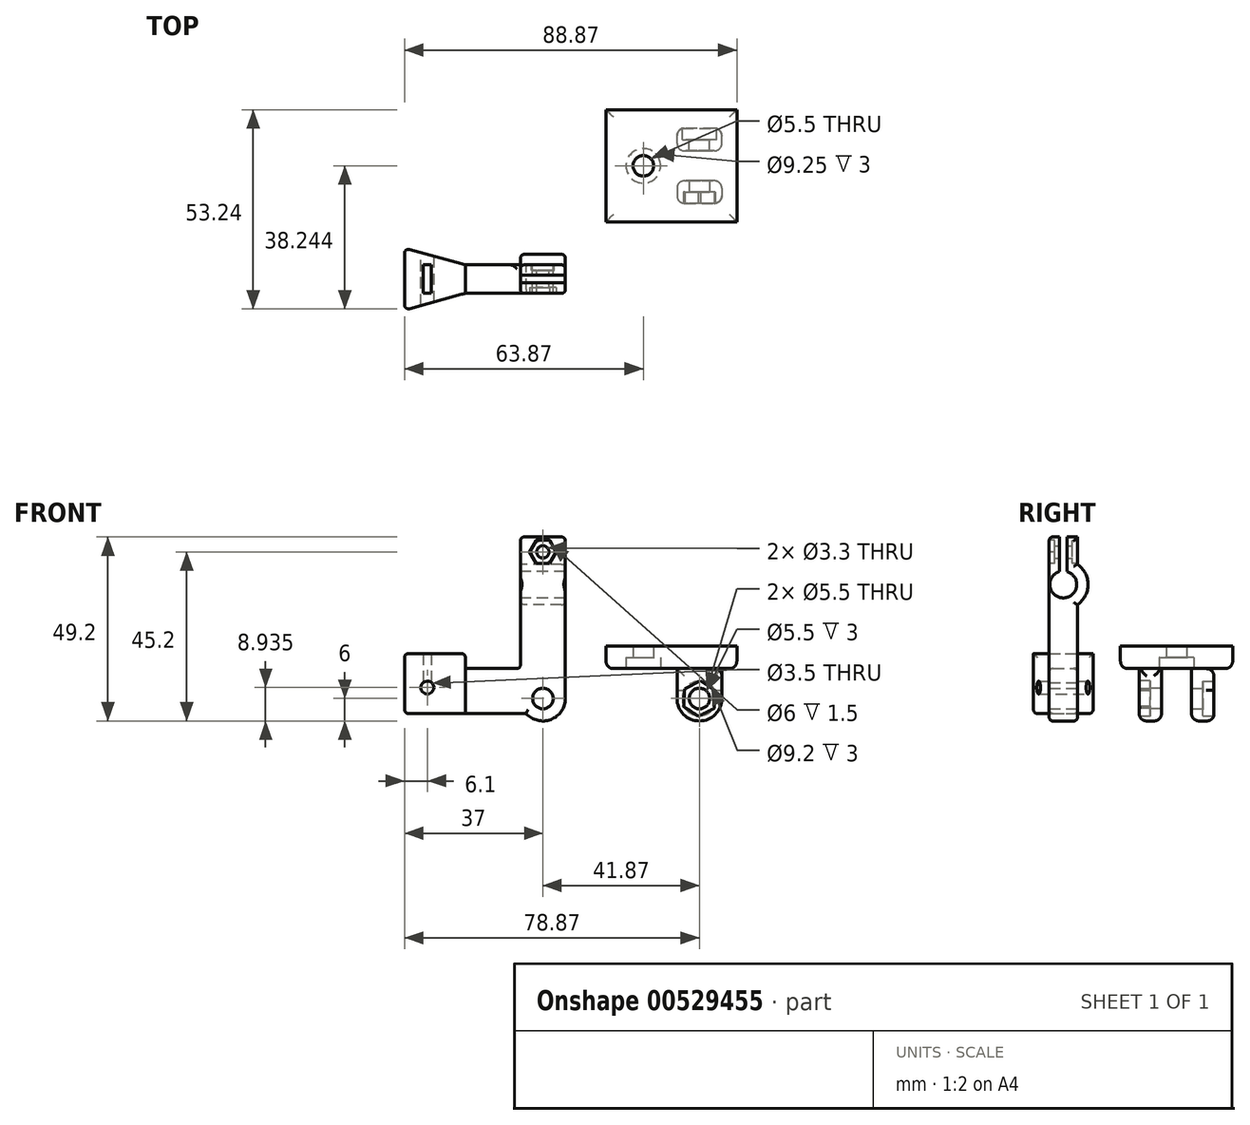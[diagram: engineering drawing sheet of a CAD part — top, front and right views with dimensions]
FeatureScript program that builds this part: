
annotation { "Feature Type Name" : "Feature", "Feature Type Description" : "" }
export const myFeature = defineFeature(function(context is Context, id is Id, definition is map)
    precondition{}
    {
        {
            assignVariable(context, id + "F0", {"name" : "pivot_w", "anyValue" : 8});
        }
        {
            assignVariable(context, id + "F1", {"name" : "hole_d", "anyValue" : 7.2});
        }
        {
            var Q0;
            Q0=qCreatedBy(makeId("Top.planeOp"),FACE);
            var sketch = newSketch(context, id + "F2", { "sketchPlane" : qUnion([Q0])});
            skLineSegment(sketch, "E0.bottom", {"start": v(-46.75, 41.48) * mm, "end": v(-11.75, 41.48) * mm});
            skLineSegment(sketch, "E0.top", {"start": v(-46.75, 11.48) * mm, "end": v(-11.75, 11.48) * mm});
            skLineSegment(sketch, "E0.left", {"start": v(-46.75, 41.48) * mm, "end": v(-46.75, 11.48) * mm});
            skLineSegment(sketch, "E0.right", {"start": v(-11.75, 41.48) * mm, "end": v(-11.75, 11.48) * mm});
            skPoint(sketch, "E1", {"position": v(-36.75, 26.48) * mm});
            skPoint(sketch, "E2", {"position": v(-46.75, 26.48) * mm});
            skLineSegment(sketch, "E3", {"start": v(-46.75, 26.48) * mm, "end": v(-36.75, 26.48) * mm, "construction": true});
            skPoint(sketch, "E4", {"position": v(-21.75, 30.48) * mm});
            skPoint(sketch, "E5", {"position": v(-21.75, 22.48) * mm});
            skLineSegment(sketch, "E6", {"start": v(-21.75, 30.48) * mm, "end": v(-21.75, 41.48) * mm, "construction": true});
            skLineSegment(sketch, "E7", {"start": v(-21.75, 22.48) * mm, "end": v(-21.75, 11.48) * mm, "construction": true});
            skLineSegment(sketch, "E8", {"start": v(-21.75, 30.48) * mm, "end": v(-11.75, 30.48) * mm, "construction": true});
            skSolve(sketch);
        }
        {
            var Q0;
            Q0=makeQuery(id+"F2.imprint","IMPRINT",FACE,{"disambiguationData":[TD([[makeQuery(id+"F2.imprint","IMPRINT",EDGE,{"derivedFrom":sQuery(id+"F2.wireOp",EDGE,"E0.bottom")}),-1.0]])]});
            extrude(context, id + "F3", {"entities" : qUnion([Q0]), "depth" : 6 * mm, "offsetDistance" : 25 * mm});
        }
        {
            var Q0;
            Q0=sQuery(id+"F2.wireOp",VERTEX,"E1");
            var Q1;
            Q1=makeQuery(id+"F3.opExtrude","SWEPT_BODY",BODY,{"disambiguationData":[OSD([sQuery(id+"F2.wireOp",EDGE,"E0.bottom"),sQuery(id+"F2.wireOp",EDGE,"E0.top"),sQuery(id+"F2.wireOp",EDGE,"E0.left"),sQuery(id+"F2.wireOp",EDGE,"E0.right")])]});
            hole(context, id + "F4", {"style" : HoleStyle.C_BORE, "endStyle" : HoleEndStyle.BLIND, "oppositeDirection" : true, "holeDiameter" : 5.5 * mm, "cBoreDiameter" : 9.25 * mm, "cBoreDepth" : 3 * mm, "holeDepth" : 12.9 * mm, "isTappedThrough" : true, "tappedDepth" : 10.5 * mm, "tapClearance" : 3, "locations" : qUnion([Q0]), "scope" : qUnion([Q1])});
        }
        {
            var Q0;
            Q0=qCreatedBy(makeId("Front.planeOp"),FACE);
            var sketch = newSketch(context, id + "F5", { "sketchPlane" : qUnion([Q0])});
            skCircle(sketch, "E9", {"center": v(-35.54, -8) * mm, "radius": 6 * mm});
            skLineSegment(sketch, "E10.bottom", {"start": v(-29.54, 0) * mm, "end": v(-41.54, 0) * mm});
            skLineSegment(sketch, "E10.top", {"start": v(-29.54, -8) * mm, "end": v(-41.54, -8) * mm});
            skLineSegment(sketch, "E10.left", {"start": v(-29.54, 0) * mm, "end": v(-29.54, -8) * mm});
            skLineSegment(sketch, "E10.right", {"start": v(-41.54, 0) * mm, "end": v(-41.54, -8) * mm});
            skCircle(sketch, "E11", {"center": v(-17.83, -8.12) * mm, "radius": 6 * mm});
            skLineSegment(sketch, "E12.bottom", {"start": v(-11.83, -0.12) * mm, "end": v(-23.83, -0.12) * mm});
            skLineSegment(sketch, "E12.top", {"start": v(-11.83, -8.12) * mm, "end": v(-23.83, -8.12) * mm});
            skLineSegment(sketch, "E12.left", {"start": v(-11.83, -0.12) * mm, "end": v(-11.83, -8.12) * mm});
            skLineSegment(sketch, "E12.right", {"start": v(-23.83, -0.12) * mm, "end": v(-23.83, -8.12) * mm});
            skCircle(sketch, "E13", {"center": v(-35.54, -8) * mm, "radius": 2.75 * mm});
            skCircle(sketch, "E14", {"center": v(-35.54, -8) * mm, "radius": 4.6 * mm});
            skCircle(sketch, "E15", {"center": v(-17.83, -8.12) * mm, "radius": 2.75 * mm});
            skCircle(sketch, "E16.cCircle", {"center": v(-17.83, -8.12) * mm, "radius": 4.1 * mm, "construction": true});
            skLineSegment(sketch, "E16.0", {"start": v(-17.54, -12.85) * mm, "end": v(-21.78, -10.74) * mm});
            skLineSegment(sketch, "E16.1", {"start": v(-21.78, -10.74) * mm, "end": v(-22.07, -6.01) * mm});
            skLineSegment(sketch, "E16.2", {"start": v(-22.07, -6.01) * mm, "end": v(-18.12, -3.4) * mm});
            skLineSegment(sketch, "E16.3", {"start": v(-18.12, -3.4) * mm, "end": v(-13.89, -5.5) * mm});
            skLineSegment(sketch, "E16.4", {"start": v(-13.89, -5.5) * mm, "end": v(-13.6, -10.23) * mm});
            skLineSegment(sketch, "E16.5", {"start": v(-13.6, -10.23) * mm, "end": v(-17.54, -12.85) * mm});
            skPoint(sketch, "E16.0.midPoint", {"position": v(-19.66, -11.8) * mm});
            skCircle(sketch, "E17", {"center": v(-63.62, -8) * mm, "radius": 6 * mm});
            skLineSegment(sketch, "E18.bottom", {"start": v(-57.62, 35.2) * mm, "end": v(-69.62, 35.2) * mm});
            skLineSegment(sketch, "E18.top", {"start": v(-57.62, -8) * mm, "end": v(-69.62, -8) * mm});
            skLineSegment(sketch, "E18.left", {"start": v(-57.62, 35.2) * mm, "end": v(-57.62, -8) * mm});
            skLineSegment(sketch, "E18.right", {"start": v(-69.62, 35.2) * mm, "end": v(-69.62, -8) * mm});
            skCircle(sketch, "E19", {"center": v(-63.62, -8) * mm, "radius": 2.75 * mm});
            skLineSegment(sketch, "E20.bottom", {"start": v(-69.62, -8) * mm, "end": v(-100.62, -8) * mm});
            skLineSegment(sketch, "E20.right", {"start": v(-100.62, -8) * mm, "end": v(-100.62, 0) * mm});
            skLineSegment(sketch, "E21.top", {"start": v(-100.62, 4) * mm, "end": v(-84.62, 4) * mm});
            skLineSegment(sketch, "E21.left", {"start": v(-100.62, 0) * mm, "end": v(-100.62, 4) * mm});
            skLineSegment(sketch, "E21.right", {"start": v(-84.62, 0) * mm, "end": v(-84.62, 4) * mm});
            skLineSegment(sketch, "E22", {"start": v(-84.62, 0) * mm, "end": v(-69.62, 0) * mm});
            skLineSegment(sketch, "E23.bottom", {"start": v(-95.62, 4) * mm, "end": v(-93.42, 4) * mm});
            skLineSegment(sketch, "E23.top", {"start": v(-95.62, -3.7) * mm, "end": v(-93.42, -3.7) * mm});
            skLineSegment(sketch, "E23.left", {"start": v(-95.62, 4) * mm, "end": v(-95.62, -3.7) * mm});
            skLineSegment(sketch, "E23.right", {"start": v(-93.42, 4) * mm, "end": v(-93.42, -3.7) * mm});
            skPoint(sketch, "E24", {"position": v(-63.62, 31.2) * mm});
            skPoint(sketch, "E24.positionSnap0", {"position": v(-63.62, 35.2) * mm});
            skLineSegment(sketch, "E25.bottom", {"start": v(-67.67, 25) * mm, "end": v(-66.17, 25) * mm});
            skLineSegment(sketch, "E25.top", {"start": v(-67.67, 20) * mm, "end": v(-66.17, 20) * mm});
            skLineSegment(sketch, "E25.left", {"start": v(-67.67, 25) * mm, "end": v(-67.67, 20) * mm});
            skLineSegment(sketch, "E25.right", {"start": v(-66.17, 25) * mm, "end": v(-66.17, 20) * mm});
            skLineSegment(sketch, "E26.1.0.0", {"start": v(-64.37, 20) * mm, "end": v(-62.87, 20) * mm});
            skLineSegment(sketch, "E26.1.0.1", {"start": v(-62.87, 25) * mm, "end": v(-62.87, 20) * mm});
            skLineSegment(sketch, "E26.1.0.2", {"start": v(-64.37, 25) * mm, "end": v(-64.37, 20) * mm});
            skLineSegment(sketch, "E26.1.0.3", {"start": v(-64.37, 25) * mm, "end": v(-62.87, 25) * mm});
            skLineSegment(sketch, "E26.2.0.0", {"start": v(-61.07, 20) * mm, "end": v(-59.57, 20) * mm});
            skLineSegment(sketch, "E26.2.0.1", {"start": v(-59.57, 25) * mm, "end": v(-59.57, 20) * mm});
            skLineSegment(sketch, "E26.2.0.2", {"start": v(-61.07, 25) * mm, "end": v(-61.07, 20) * mm});
            skLineSegment(sketch, "E26.2.0.3", {"start": v(-61.07, 25) * mm, "end": v(-59.57, 25) * mm});
            skLineSegment(sketch, "E26.direction1", {"start": v(-67.67, 20) * mm, "end": v(-64.37, 20) * mm, "construction": true});
            skLineSegment(sketch, "E27", {"start": v(-64.94, 35.2) * mm, "end": v(-64.94, 25) * mm, "construction": true});
            skLineSegment(sketch, "E28", {"start": v(-67.67, 25) * mm, "end": v(-69.62, 25) * mm, "construction": true});
            skLineSegment(sketch, "E29", {"start": v(-59.57, 25) * mm, "end": v(-57.62, 25) * mm, "construction": true});
            skLineSegment(sketch, "E30", {"start": v(-67.67, 22.5) * mm, "end": v(-69.62, 22.5) * mm, "construction": true});
            skCircle(sketch, "E31", {"center": v(-94.52, -5.06) * mm, "radius": 1.75 * mm});
            skLineSegment(sketch, "E32", {"start": v(-68.1, -12) * mm, "end": v(-100.62, -12) * mm});
            skLineSegment(sketch, "E33", {"start": v(-100.62, -12) * mm, "end": v(-100.62, -8) * mm});
            skLineSegment(sketch, "E34", {"start": v(-100.62, -2) * mm, "end": v(-95.62, -2) * mm, "construction": true});
            skSolve(sketch);
        }
        {
            var Q0;
            Q0=makeQuery(id+"F5.imprint","IMPRINT",FACE,{"disambiguationData":[TD([[makeQuery(id+"F5.imprint","IMPRINT",EDGE,{"derivedFrom":sQuery(id+"F5.wireOp",EDGE,"E10.bottom")}),1.0]])]});
            var Q1;
            {var subQ0=sQuery(id+"F5.wireOp",EDGE,"E14");var subQ1=sQuery(id+"F5.wireOp",EDGE,"E10.top");var subQ2=makeQuery(id+"F5.imprint","INTERSECT",VERTEX,{"disambiguationData":[OD(0.0)],"derivedFrom":[subQ1,subQ0]});Q1=makeQuery(id+"F5.imprint","IMPRINT",FACE,{"disambiguationData":[TD([[makeQuery(id+"F5.imprint","IMPRINT",EDGE,{"disambiguationData":[TD([[subQ2,-1.0]])],"derivedFrom":subQ1}),-1.0]])]});}
            var Q2;
            {var subQ0=sQuery(id+"F5.wireOp",EDGE,"E10.top");var subQ4=sQuery(id+"F5.wireOp",EDGE,"E14");var subQ5=makeQuery(id+"F5.imprint","INTERSECT",VERTEX,{"disambiguationData":[OD(0.0)],"derivedFrom":[subQ0,subQ4]});Q2=makeQuery(id+"F5.imprint","IMPRINT",FACE,{"disambiguationData":[TD([[makeQuery(id+"F5.imprint","IMPRINT",EDGE,{"disambiguationData":[TD([[subQ5,1.0]])],"derivedFrom":subQ4}),-1.0]])]});}
            var Q3;
            {var subQ0=sQuery(id+"F5.wireOp",EDGE,"E14");var subQ1=sQuery(id+"F5.wireOp",EDGE,"E10.top");var subQ2=makeQuery(id+"F5.imprint","INTERSECT",VERTEX,{"disambiguationData":[OD(0.0)],"derivedFrom":[subQ1,subQ0]});Q3=makeQuery(id+"F5.imprint","IMPRINT",FACE,{"disambiguationData":[TD([[makeQuery(id+"F5.imprint","IMPRINT",EDGE,{"disambiguationData":[TD([[subQ2,-1.0]])],"derivedFrom":subQ1}),1.0]])]});}
            var Q4;
            {var subQ0=sQuery(id+"F5.wireOp",EDGE,"E10.top");var subQ4=sQuery(id+"F5.wireOp",EDGE,"E14");var subQ5=makeQuery(id+"F5.imprint","INTERSECT",VERTEX,{"disambiguationData":[OD(0.0)],"derivedFrom":[subQ0,subQ4]});Q4=makeQuery(id+"F5.imprint","IMPRINT",FACE,{"disambiguationData":[TD([[makeQuery(id+"F5.imprint","IMPRINT",EDGE,{"disambiguationData":[TD([[subQ5,-1.0]])],"derivedFrom":subQ4}),-1.0]])]});}
            var Q5;
            Q5=makeQuery(id+"F5.imprint","IMPRINT",FACE,{"disambiguationData":[TD([[makeQuery(id+"F5.imprint","IMPRINT",EDGE,{"derivedFrom":sQuery(id+"F5.wireOp",EDGE,"E12.bottom")}),1.0]])]});
            var Q6;
            {var subQ5=sQuery(id+"F5.wireOp",EDGE,"E16.2");Q6=makeQuery(id+"F5.imprint","IMPRINT",FACE,{"disambiguationData":[TD([[makeQuery(id+"F5.imprint","IMPRINT",EDGE,{"derivedFrom":subQ5}),1.0]])]});}
            var Q7;
            {var subQ0=sQuery(id+"F5.wireOp",EDGE,"E16.2");Q7=makeQuery(id+"F5.imprint","IMPRINT",FACE,{"disambiguationData":[TD([[makeQuery(id+"F5.imprint","IMPRINT",EDGE,{"derivedFrom":subQ0}),-1.0]])]});}
            var Q8;
            {var subQ8=sQuery(id+"F5.wireOp",EDGE,"E16.0");Q8=makeQuery(id+"F5.imprint","IMPRINT",FACE,{"disambiguationData":[TD([[makeQuery(id+"F5.imprint","IMPRINT",EDGE,{"derivedFrom":subQ8}),1.0]])]});}
            var Q9;
            {var subQ6=sQuery(id+"F5.wireOp",EDGE,"E16.0");Q9=makeQuery(id+"F5.imprint","IMPRINT",FACE,{"disambiguationData":[TD([[makeQuery(id+"F5.imprint","IMPRINT",EDGE,{"derivedFrom":subQ6}),-1.0]])]});}
            extrude(context, id + "F6", {"entities" : qUnion([Q0, Q1, Q2, Q3, Q4, Q5, Q6, Q7, Q8, Q9]), "depth" : 6 * mm, "offsetDistance" : 25 * mm});
        }
        {
            var Q0;
            {var subQ0=sQuery(id+"F5.wireOp",EDGE,"E16.2");Q0=makeQuery(id+"F5.imprint","IMPRINT",FACE,{"disambiguationData":[TD([[makeQuery(id+"F5.imprint","IMPRINT",EDGE,{"derivedFrom":subQ0}),-1.0]])]});}
            var Q1;
            {var subQ6=sQuery(id+"F5.wireOp",EDGE,"E16.0");Q1=makeQuery(id+"F5.imprint","IMPRINT",FACE,{"disambiguationData":[TD([[makeQuery(id+"F5.imprint","IMPRINT",EDGE,{"derivedFrom":subQ6}),-1.0]])]});}
            var Q2;
            {var subQ0=sQuery(id+"F5.wireOp",EDGE,"E14");var subQ1=sQuery(id+"F5.wireOp",EDGE,"E10.top");var subQ2=makeQuery(id+"F5.imprint","INTERSECT",VERTEX,{"disambiguationData":[OD(0.0)],"derivedFrom":[subQ1,subQ0]});Q2=makeQuery(id+"F5.imprint","IMPRINT",FACE,{"disambiguationData":[TD([[makeQuery(id+"F5.imprint","IMPRINT",EDGE,{"disambiguationData":[TD([[subQ2,-1.0]])],"derivedFrom":subQ1}),1.0]])]});}
            var Q3;
            {var subQ0=sQuery(id+"F5.wireOp",EDGE,"E14");var subQ1=sQuery(id+"F5.wireOp",EDGE,"E10.top");var subQ2=makeQuery(id+"F5.imprint","INTERSECT",VERTEX,{"disambiguationData":[OD(0.0)],"derivedFrom":[subQ1,subQ0]});Q3=makeQuery(id+"F5.imprint","IMPRINT",FACE,{"disambiguationData":[TD([[makeQuery(id+"F5.imprint","IMPRINT",EDGE,{"disambiguationData":[TD([[subQ2,-1.0]])],"derivedFrom":subQ1}),-1.0]])]});}
            extrude(context, id + "F7", {"entities" : qUnion([Q0, Q1, Q2, Q3]), "operationType" : NewBodyOperationType.REMOVE, "depth" : 3 * mm, "offsetDistance" : 25 * mm});
        }
        {
            var Q0;
            Q0=makeQuery(id+"F6.opExtrude","CAP_EDGE",EDGE,{"disambiguationData":[OSD([sQuery(id+"F5.wireOp",EDGE,"E10.bottom")])],"isStart":false});
            cPoint(context, id + "F8", {"entities" : qUnion([Q0]), "parameter" : 0.5});
        }
        {
            var Q0;
            Q0=makeQuery(id+"F6.opExtrude","SWEPT_BODY",BODY,{"disambiguationData":[OSD([sQuery(id+"F5.wireOp",EDGE,"E9"),sQuery(id+"F5.wireOp",EDGE,"E10.bottom"),sQuery(id+"F5.wireOp",EDGE,"E10.left"),sQuery(id+"F5.wireOp",EDGE,"E10.right"),sQuery(id+"F5.wireOp",EDGE,"E13")])]});
            var Q1;
            Q1=qCreatedBy(id+"F8",VERTEX);
            var Q2;
            Q2=sQuery(id+"F2.wireOp",VERTEX,"E6.start");
            transform(context, id + "F9", {"entities" : qUnion([Q0]), "transformType" : TransformType.TRANSLATION_ENTITY, "oppositeDirectionEntity" : false, "transformLine" : qUnion([Q1, Q2]), "makeCopy" : false});
        }
        {
            var Q0;
            Q0=makeQuery(id+"F6.opExtrude","SWEPT_BODY",BODY,{"disambiguationData":[OSD([sQuery(id+"F5.wireOp",EDGE,"E11"),sQuery(id+"F5.wireOp",EDGE,"E12.bottom"),sQuery(id+"F5.wireOp",EDGE,"E12.left"),sQuery(id+"F5.wireOp",EDGE,"E12.right"),sQuery(id+"F5.wireOp",EDGE,"E15")])]});
            var Q1;
            Q1=sQuery(id+"F5.wireOp",EDGE,"E12.left");
            transform(context, id + "F10", {"entities" : qUnion([Q0]), "transformType" : TransformType.ROTATION, "transformAxis" : qUnion([Q1]), "angle" : 180 * degree, "makeCopy" : false});
        }
        {
            var Q0;
            Q0=makeQuery(id+"F6.opExtrude","CAP_EDGE",EDGE,{"disambiguationData":[OSD([sQuery(id+"F5.wireOp",EDGE,"E12.bottom")])],"isStart":false});
            cPoint(context, id + "F11", {"entities" : qUnion([Q0]), "parameter" : 0.5});
        }
        {
            var Q0;
            Q0=makeQuery(id+"F6.opExtrude","SWEPT_BODY",BODY,{"disambiguationData":[OSD([sQuery(id+"F5.wireOp",EDGE,"E11"),sQuery(id+"F5.wireOp",EDGE,"E12.bottom"),sQuery(id+"F5.wireOp",EDGE,"E12.left"),sQuery(id+"F5.wireOp",EDGE,"E12.right"),sQuery(id+"F5.wireOp",EDGE,"E15")])]});
            var Q1;
            Q1=qCreatedBy(id+"F11",VERTEX);
            var Q2;
            Q2=sQuery(id+"F2.wireOp",VERTEX,"E7.start");
            transform(context, id + "F12", {"entities" : qUnion([Q0]), "transformType" : TransformType.TRANSLATION_ENTITY, "oppositeDirectionEntity" : false, "transformLine" : qUnion([Q1, Q2]), "makeCopy" : false});
        }
        {
            var Q0;
            {var subQ0=sQuery(id+"F5.wireOp",EDGE,"E18.top");var subQ4=sQuery(id+"F5.wireOp",EDGE,"E19");var subQ5=makeQuery(id+"F5.imprint","INTERSECT",VERTEX,{"disambiguationData":[OD(0.0)],"derivedFrom":[subQ0,subQ4]});Q0=makeQuery(id+"F5.imprint","IMPRINT",FACE,{"disambiguationData":[TD([[makeQuery(id+"F5.imprint","IMPRINT",EDGE,{"disambiguationData":[TD([[subQ5,1.0]])],"derivedFrom":subQ4}),-1.0]])]});}
            var Q1;
            {var subQ0=sQuery(id+"F5.wireOp",EDGE,"E18.top");var subQ4=sQuery(id+"F5.wireOp",EDGE,"E19");var subQ6=makeQuery(id+"F5.imprint","INTERSECT",VERTEX,{"disambiguationData":[OD(0.0)],"derivedFrom":[subQ0,subQ4]});Q1=makeQuery(id+"F5.imprint","IMPRINT",FACE,{"disambiguationData":[TD([[makeQuery(id+"F5.imprint","IMPRINT",EDGE,{"disambiguationData":[TD([[subQ6,-1.0]])],"derivedFrom":subQ4}),-1.0]])]});}
            var Q2;
            Q2=qSketchRegion(id+"F14",true);
            var Q3;
            {var subQ0=sQuery(id+"F5.wireOp",EDGE,"E18.bottom");Q3=makeQuery(id+"F5.imprint","IMPRINT",FACE,{"disambiguationData":[TD([[makeQuery(id+"F5.imprint","IMPRINT",EDGE,{"derivedFrom":subQ0}),1.0]])]});}
            var Q4;
            Q4=makeQuery(id+"F5.imprint","IMPRINT",FACE,{"disambiguationData":[TD([[makeQuery(id+"F5.imprint","IMPRINT",EDGE,{"derivedFrom":sQuery(id+"F5.wireOp",EDGE,"E26.2.0.0")}),1.0]])]});
            var Q5;
            Q5=makeQuery(id+"F5.imprint","IMPRINT",FACE,{"disambiguationData":[TD([[makeQuery(id+"F5.imprint","IMPRINT",EDGE,{"derivedFrom":sQuery(id+"F5.wireOp",EDGE,"E26.1.0.0")}),1.0]])]});
            var Q6;
            Q6=makeQuery(id+"F5.imprint","IMPRINT",FACE,{"disambiguationData":[TD([[makeQuery(id+"F5.imprint","IMPRINT",EDGE,{"derivedFrom":sQuery(id+"F5.wireOp",EDGE,"E25.bottom")}),-1.0]])]});
            var Q7;
            {var subQ0=sQuery(id+"F5.wireOp",EDGE,"E20.bottom");Q7=makeQuery(id+"F5.imprint","IMPRINT",FACE,{"disambiguationData":[TD([[makeQuery(id+"F5.imprint","IMPRINT",EDGE,{"derivedFrom":subQ0}),1.0]])]});}
            var Q8;
            {var subQ0=sQuery(id+"F5.wireOp",EDGE,"E21.right");Q8=makeQuery(id+"F5.imprint","IMPRINT",FACE,{"disambiguationData":[TD([[makeQuery(id+"F5.imprint","IMPRINT",EDGE,{"derivedFrom":subQ0}),1.0]])]});}
            var Q9;
            {var subQ6=sQuery(id+"F5.wireOp",EDGE,"E20.right");Q9=makeQuery(id+"F5.imprint","IMPRINT",FACE,{"disambiguationData":[TD([[makeQuery(id+"F5.imprint","IMPRINT",EDGE,{"derivedFrom":subQ6}),-1.0]])]});}
            extrude(context, id + "F13", {"entities" : qUnion([Q0, Q1, Q2, Q3, Q4, Q5, Q6, Q7, Q8, Q9]), "depth" : (getVariable(context, 'pivot_w') - 0.4) * mm, "offsetDistance" : 25 * mm});
        }
        {
            var Q0;
            Q0=makeQuery(id+"F13.opExtrude","SWEPT_FACE",FACE,{"disambiguationData":[OSD([sQuery(id+"F5.wireOp",EDGE,"E18.right")])]});
            var sketch = newSketch(context, id + "F14", { "sketchPlane" : qUnion([Q0])});
            skPoint(sketch, "E35", {"position": v(3.8, 22.5) * mm});
            skPoint(sketch, "E35.positionSnap0", {"position": v(3.8, 35.2) * mm});
            skPoint(sketch, "E36", {"position": v(0, 22.5) * mm});
            skLineSegment(sketch, "E37.bottom", {"start": v(2.8, 35.2) * mm, "end": v(4.8, 35.2) * mm});
            skLineSegment(sketch, "E37.top", {"start": v(2.8, 19.4) * mm, "end": v(4.8, 19.4) * mm});
            skLineSegment(sketch, "E37.left", {"start": v(2.8, 35.2) * mm, "end": v(2.8, 19.4) * mm});
            skLineSegment(sketch, "E37.right", {"start": v(4.8, 35.2) * mm, "end": v(4.8, 19.4) * mm});
            skLineSegment(sketch, "E38", {"start": v(2.8, 29.82) * mm, "end": v(0, 29.82) * mm});
            skLineSegment(sketch, "E39", {"start": v(4.8, 29.9) * mm, "end": v(7.6, 29.9) * mm});
            skLineSegment(sketch, "E40", {"start": v(3.8, 22.5) * mm, "end": v(0, 22.5) * mm, "construction": true});
            skCircle(sketch, "E41", {"center": v(3.8, 22.5) * mm, "radius": 6.6 * mm});
            skSolve(sketch);
        }
        {
            var Q0;
            {var subQ0=sQuery(id+"F14.wireOp",EDGE,"E41");var subQ1=makeQuery(id+"F13.opExtrude","CAP_EDGE",EDGE,{"disambiguationData":[OSD([sQuery(id+"F5.wireOp",EDGE,"E18.right")])],"isStart":true});var subQ2=makeQuery(id+"F14.imprint","INTERSECT",VERTEX,{"disambiguationData":[OD(0.0)],"derivedFrom":[subQ1,subQ0]});Q0=makeQuery(id+"F14.imprint","IMPRINT",FACE,{"disambiguationData":[TD([[makeQuery(id+"F14.imprint","IMPRINT",EDGE,{"disambiguationData":[TD([[subQ2,-1.0]])],"derivedFrom":subQ0}),1.0]])]});}
            var Q1;
            {var subQ0=sQuery(id+"F14.wireOp",EDGE,"E41");var subQ1=makeQuery(id+"F13.opExtrude","CAP_EDGE",EDGE,{"disambiguationData":[OSD([sQuery(id+"F5.wireOp",EDGE,"E18.right")])],"isStart":false});var subQ2=makeQuery(id+"F14.imprint","INTERSECT",VERTEX,{"disambiguationData":[OD(0.0)],"derivedFrom":[subQ1,subQ0]});Q1=makeQuery(id+"F14.imprint","IMPRINT",FACE,{"disambiguationData":[TD([[makeQuery(id+"F14.imprint","IMPRINT",EDGE,{"disambiguationData":[TD([[subQ2,1.0]])],"derivedFrom":subQ0}),1.0]])]});}
            extrude(context, id + "F15", {"entities" : qUnion([Q0, Q1]), "operationType" : NewBodyOperationType.ADD, "oppositeDirection" : true, "depth" : 12 * mm, "offsetDistance" : 25 * mm});
        }
        {
            var Q0;
            {var subQ4=sQuery(id+"F14.wireOp",EDGE,"E37.bottom");Q0=makeQuery(id+"F14.imprint","IMPRINT",FACE,{"disambiguationData":[TD([[makeQuery(id+"F14.imprint","IMPRINT",EDGE,{"derivedFrom":subQ4}),1.0]])]});}
            var Q1;
            {var subQ0=sQuery(id+"F14.wireOp",EDGE,"E37.top");Q1=makeQuery(id+"F14.imprint","IMPRINT",FACE,{"disambiguationData":[TD([[makeQuery(id+"F14.imprint","IMPRINT",EDGE,{"derivedFrom":subQ0}),1.0]])]});}
            extrude(context, id + "F16", {"entities" : qUnion([Q0, Q1]), "operationType" : NewBodyOperationType.REMOVE, "oppositeDirection" : true, "depth" : 12 * mm, "offsetDistance" : 25 * mm});
        }
        {
            var Q0;
            Q0=sQuery(id+"F14.wireOp",VERTEX,"E35");
            var Q1;
            Q1=makeQuery(id+"F13.opExtrude","SWEPT_BODY",BODY,{"disambiguationData":[OSD([sQuery(id+"F5.wireOp",EDGE,"E17"),sQuery(id+"F5.wireOp",EDGE,"E18.bottom"),sQuery(id+"F5.wireOp",EDGE,"E18.left"),sQuery(id+"F5.wireOp",EDGE,"E18.right"),sQuery(id+"F5.wireOp",EDGE,"E19"),sQuery(id+"F5.wireOp",EDGE,"E20.bottom"),sQuery(id+"F5.wireOp",EDGE,"E20.right"),sQuery(id+"F5.wireOp",EDGE,"E21.top"),sQuery(id+"F5.wireOp",EDGE,"E21.left"),sQuery(id+"F5.wireOp",EDGE,"E21.right"),sQuery(id+"F5.wireOp",EDGE,"E22"),sQuery(id+"F5.wireOp",EDGE,"E23.top"),sQuery(id+"F5.wireOp",EDGE,"E23.left"),sQuery(id+"F5.wireOp",EDGE,"E23.right"),sQuery(id+"F5.wireOp",EDGE,"E25.bottom"),sQuery(id+"F5.wireOp",EDGE,"E25.top"),sQuery(id+"F5.wireOp",EDGE,"E25.left"),sQuery(id+"F5.wireOp",EDGE,"E25.right"),sQuery(id+"F5.wireOp",EDGE,"E26.1.0.0"),sQuery(id+"F5.wireOp",EDGE,"E26.1.0.1"),sQuery(id+"F5.wireOp",EDGE,"E26.1.0.2"),sQuery(id+"F5.wireOp",EDGE,"E26.1.0.3"),sQuery(id+"F5.wireOp",EDGE,"E26.2.0.0"),sQuery(id+"F5.wireOp",EDGE,"E26.2.0.1"),sQuery(id+"F5.wireOp",EDGE,"E26.2.0.2"),sQuery(id+"F5.wireOp",EDGE,"E26.2.0.3")])]});
            hole(context, id + "F17", {"style" : HoleStyle.SIMPLE, "endStyle" : HoleEndStyle.BLIND, "holeDiameter" : (getVariable(context, 'hole_d')) * mm, "holeDepth" : 30 * mm, "isTappedThrough" : true, "tappedDepth" : 10.5 * mm, "tapClearance" : 3, "locations" : qUnion([Q0]), "scope" : qUnion([Q1])});
        }
        {
            var Q0;
            Q0=sQuery(id+"F5.wireOp",VERTEX,"E24");
            var Q1;
            Q1=makeQuery(id+"F13.opExtrude","SWEPT_BODY",BODY,{"disambiguationData":[OSD([sQuery(id+"F5.wireOp",EDGE,"E17"),sQuery(id+"F5.wireOp",EDGE,"E18.bottom"),sQuery(id+"F5.wireOp",EDGE,"E18.left"),sQuery(id+"F5.wireOp",EDGE,"E18.right"),sQuery(id+"F5.wireOp",EDGE,"E19"),sQuery(id+"F5.wireOp",EDGE,"E20.bottom"),sQuery(id+"F5.wireOp",EDGE,"E20.right"),sQuery(id+"F5.wireOp",EDGE,"E21.top"),sQuery(id+"F5.wireOp",EDGE,"E21.left"),sQuery(id+"F5.wireOp",EDGE,"E21.right"),sQuery(id+"F5.wireOp",EDGE,"E22"),sQuery(id+"F5.wireOp",EDGE,"E23.top"),sQuery(id+"F5.wireOp",EDGE,"E23.left"),sQuery(id+"F5.wireOp",EDGE,"E23.right"),sQuery(id+"F5.wireOp",EDGE,"E25.bottom"),sQuery(id+"F5.wireOp",EDGE,"E25.top"),sQuery(id+"F5.wireOp",EDGE,"E25.left"),sQuery(id+"F5.wireOp",EDGE,"E25.right"),sQuery(id+"F5.wireOp",EDGE,"E26.1.0.0"),sQuery(id+"F5.wireOp",EDGE,"E26.1.0.1"),sQuery(id+"F5.wireOp",EDGE,"E26.1.0.2"),sQuery(id+"F5.wireOp",EDGE,"E26.1.0.3"),sQuery(id+"F5.wireOp",EDGE,"E26.2.0.0"),sQuery(id+"F5.wireOp",EDGE,"E26.2.0.1"),sQuery(id+"F5.wireOp",EDGE,"E26.2.0.2"),sQuery(id+"F5.wireOp",EDGE,"E26.2.0.3")])]});
            hole(context, id + "F18", {"style" : HoleStyle.C_BORE, "endStyle" : HoleEndStyle.BLIND, "oppositeDirection" : true, "holeDiameter" : 3.3 * mm, "cBoreDiameter" : 6 * mm, "cBoreDepth" : 1.5 * mm, "holeDepth" : 31 * mm, "isTappedThrough" : true, "tappedDepth" : 10.5 * mm, "tapClearance" : 3, "locations" : qUnion([Q0]), "scope" : qUnion([Q1])});
        }
        {
            var Q0;
            Q0=makeQuery(id+"F13.opExtrude","CAP_FACE",FACE,{"disambiguationData":[OSD([sQuery(id+"F5.wireOp",EDGE,"E17"),sQuery(id+"F5.wireOp",EDGE,"E18.bottom"),sQuery(id+"F5.wireOp",EDGE,"E18.left"),sQuery(id+"F5.wireOp",EDGE,"E18.right"),sQuery(id+"F5.wireOp",EDGE,"E19"),sQuery(id+"F5.wireOp",EDGE,"E20.bottom"),sQuery(id+"F5.wireOp",EDGE,"E20.right"),sQuery(id+"F5.wireOp",EDGE,"E21.top"),sQuery(id+"F5.wireOp",EDGE,"E21.left"),sQuery(id+"F5.wireOp",EDGE,"E21.right"),sQuery(id+"F5.wireOp",EDGE,"E22"),sQuery(id+"F5.wireOp",EDGE,"E23.top"),sQuery(id+"F5.wireOp",EDGE,"E23.left"),sQuery(id+"F5.wireOp",EDGE,"E23.right"),sQuery(id+"F5.wireOp",EDGE,"E25.bottom"),sQuery(id+"F5.wireOp",EDGE,"E25.top"),sQuery(id+"F5.wireOp",EDGE,"E25.left"),sQuery(id+"F5.wireOp",EDGE,"E25.right"),sQuery(id+"F5.wireOp",EDGE,"E26.1.0.0"),sQuery(id+"F5.wireOp",EDGE,"E26.1.0.1"),sQuery(id+"F5.wireOp",EDGE,"E26.1.0.2"),sQuery(id+"F5.wireOp",EDGE,"E26.1.0.3"),sQuery(id+"F5.wireOp",EDGE,"E26.2.0.0"),sQuery(id+"F5.wireOp",EDGE,"E26.2.0.1"),sQuery(id+"F5.wireOp",EDGE,"E26.2.0.2"),sQuery(id+"F5.wireOp",EDGE,"E26.2.0.3")])],"isStart":false});
            var sketch = newSketch(context, id + "F19", { "sketchPlane" : qUnion([Q0])});
            skCircle(sketch, "E42.cCircle", {"center": v(-63.62, 31.2) * mm, "radius": 3.1 * mm, "construction": true});
            skLineSegment(sketch, "E42.0", {"start": v(-65.41, 34.3) * mm, "end": v(-61.83, 34.3) * mm});
            skLineSegment(sketch, "E42.1", {"start": v(-61.83, 34.3) * mm, "end": v(-60.04, 31.2) * mm});
            skLineSegment(sketch, "E42.2", {"start": v(-60.04, 31.2) * mm, "end": v(-61.83, 28.1) * mm});
            skLineSegment(sketch, "E42.3", {"start": v(-61.83, 28.1) * mm, "end": v(-65.41, 28.1) * mm});
            skLineSegment(sketch, "E42.4", {"start": v(-65.41, 28.1) * mm, "end": v(-67.2, 31.2) * mm});
            skLineSegment(sketch, "E42.5", {"start": v(-67.2, 31.2) * mm, "end": v(-65.41, 34.3) * mm});
            skPoint(sketch, "E42.0.midPoint", {"position": v(-63.62, 34.3) * mm});
            skSolve(sketch);
        }
        {
            var Q0;
            Q0=makeQuery(id+"F19.imprint","IMPRINT",FACE,{"disambiguationData":[TD([[makeQuery(id+"F19.imprint","IMPRINT",EDGE,{"derivedFrom":sQuery(id+"F19.wireOp",EDGE,"E42.0")}),-1.0]])]});
            extrude(context, id + "F20", {"entities" : qUnion([Q0]), "operationType" : NewBodyOperationType.REMOVE, "oppositeDirection" : true, "depth" : 1.5 * mm, "offsetDistance" : 25 * mm});
        }
        {
            var Q0;
            Q0=makeQuery(id+"F6.opExtrude","SWEPT_FACE",FACE,{"disambiguationData":[OSD([sQuery(id+"F5.wireOp",EDGE,"E9")])]});
            var Q1;
            Q1=makeQuery(id+"F6.opExtrude","SWEPT_FACE",FACE,{"disambiguationData":[OSD([sQuery(id+"F5.wireOp",EDGE,"E11")])]});
            var Q2;
            Q2=makeQuery(id+"F3.opExtrude","CAP_EDGE",EDGE,{"disambiguationData":[OSD([sQuery(id+"F2.wireOp",EDGE,"E0.bottom")])],"isStart":true});
            var Q3;
            Q3=makeQuery(id+"F3.opExtrude","CAP_EDGE",EDGE,{"disambiguationData":[OSD([sQuery(id+"F2.wireOp",EDGE,"E0.right")])],"isStart":true});
            var Q4;
            Q4=makeQuery(id+"F3.opExtrude","CAP_EDGE",EDGE,{"disambiguationData":[OSD([sQuery(id+"F2.wireOp",EDGE,"E0.top")])],"isStart":true});
            var Q5;
            Q5=makeQuery(id+"F3.opExtrude","CAP_EDGE",EDGE,{"disambiguationData":[OSD([sQuery(id+"F2.wireOp",EDGE,"E0.left")])],"isStart":true});
            var Q6;
            Q6=makeQuery(id+"F6.opExtrude","CAP_EDGE",EDGE,{"disambiguationData":[OSD([sQuery(id+"F5.wireOp",EDGE,"E10.bottom")])],"isStart":true});
            var Q7;
            Q7=makeQuery(id+"F6.opExtrude","SWEPT_EDGE",EDGE,{"disambiguationData":[OSD([sQuery(id+"F5.wireOp",EDGE,"E12.bottom"),sQuery(id+"F5.wireOp",EDGE,"E12.right")])]});
            fillet(context, id + "F21", {"entities" : qUnion([Q0, Q1, Q2, Q3, Q4, Q5, Q6, Q7]), "radius" : 2 * mm, "tangentPropagation" : true, "allowEdgeOverflow" : false});
        }
        {
            var Q0;
            Q0=makeQuery(id+"F13.opExtrude","SWEPT_FACE",FACE,{"disambiguationData":[OSD([sQuery(id+"F5.wireOp",EDGE,"E32")])]});
            var sketch = newSketch(context, id + "F22", { "sketchPlane" : qUnion([Q0])});
            skLineSegment(sketch, "E43", {"start": v(-84.36, 0) * mm, "end": v(-100.62, -4.47) * mm});
            skLineSegment(sketch, "E44", {"start": v(-100.62, 0) * mm, "end": v(-100.62, -4.47) * mm});
            skLineSegment(sketch, "E45", {"start": v(-84.36, 7.6) * mm, "end": v(-100.62, 12.07) * mm});
            skLineSegment(sketch, "E46", {"start": v(-100.62, 12.07) * mm, "end": v(-100.62, 7.6) * mm});
            skSolve(sketch);
        }
        {
            var Q0;
            {var subQ0=sQuery(id+"F22.wireOp",EDGE,"E45");Q0=makeQuery(id+"F22.imprint","IMPRINT",FACE,{"disambiguationData":[TD([[makeQuery(id+"F22.imprint","IMPRINT",EDGE,{"derivedFrom":subQ0}),1.0]])]});}
            var Q1;
            {var subQ0=sQuery(id+"F22.wireOp",EDGE,"E43");Q1=makeQuery(id+"F22.imprint","IMPRINT",FACE,{"disambiguationData":[TD([[makeQuery(id+"F22.imprint","IMPRINT",EDGE,{"derivedFrom":subQ0}),-1.0]])]});}
            var Q2;
            {var subQ0=sQuery(id+"F5.wireOp",EDGE,"E21.top");Q2=makeQuery(id+"F13.opExtrude","SWEPT_FACE",FACE,{"disambiguationData":[OSD([subQ0]),TDD([makeQuery(id+"F5.imprint","IMPRINT",EDGE,{"disambiguationData":[TD([[makeQuery(id+"F5.imprint","INTERSECT",VERTEX,{"derivedFrom":[subQ0,sQuery(id+"F5.wireOp",EDGE,"E21.left")]}),-1.0]])],"derivedFrom":subQ0})])]});}
            extrude(context, id + "F23", {"entities" : qUnion([Q0, Q1]), "operationType" : NewBodyOperationType.ADD, "endBound" : BoundingType.UP_TO_SURFACE, "oppositeDirection" : true, "depth" : 16 * mm, "endBoundEntityFace" : qUnion([Q2]), "offsetDistance" : 25 * mm});
        }
        {
            var Q0;
            Q0=makeQuery(id+"F13.opExtrude","SWEPT_FACE",FACE,{"disambiguationData":[OSD([sQuery(id+"F5.wireOp",EDGE,"E22")])]});
            var sketch = newSketch(context, id + "F24", { "sketchPlane" : qUnion([Q0])});
            skLineSegment(sketch, "E47.bottom", {"start": v(-84.36, -7.6) * mm, "end": v(-84.62, -7.6) * mm});
            skLineSegment(sketch, "E47.top", {"start": v(-84.36, 0) * mm, "end": v(-84.62, 0) * mm});
            skLineSegment(sketch, "E47.left", {"start": v(-84.36, -7.6) * mm, "end": v(-84.36, 0) * mm});
            skLineSegment(sketch, "E47.right", {"start": v(-84.62, -7.6) * mm, "end": v(-84.62, 0) * mm});
            skSolve(sketch);
        }
        {
            var Q0;
            Q0=makeQuery(id+"F24.imprint","IMPRINT",FACE,{"disambiguationData":[TD([[makeQuery(id+"F24.imprint","IMPRINT",EDGE,{"derivedFrom":sQuery(id+"F24.wireOp",EDGE,"E47.bottom")}),1.0]])]});
            extrude(context, id + "F25", {"entities" : qUnion([Q0]), "operationType" : NewBodyOperationType.ADD, "depth" : 4 * mm, "offsetDistance" : 25 * mm});
        }
        {
            var Q0;
            {var subQ0=sQuery(id+"F5.wireOp",EDGE,"E23.top");Q0=makeQuery(id+"F5.imprint","IMPRINT",FACE,{"disambiguationData":[TD([[makeQuery(id+"F5.imprint","IMPRINT",EDGE,{"derivedFrom":subQ0}),-1.0]])]});}
            var Q1;
            Q1=makeQuery(id+"F5.imprint","IMPRINT",FACE,{"disambiguationData":[TD([[makeQuery(id+"F5.imprint","IMPRINT",EDGE,{"derivedFrom":sQuery(id+"F5.wireOp",EDGE,"E23.bottom")}),-1.0]])]});
            var Q2;
            {var subQ0=sQuery(id+"F5.wireOp",EDGE,"E23.top");Q2=makeQuery(id+"F5.imprint","IMPRINT",FACE,{"disambiguationData":[TD([[makeQuery(id+"F5.imprint","IMPRINT",EDGE,{"derivedFrom":subQ0}),1.0]])]});}
            extrude(context, id + "F26", {"entities" : qUnion([Q0, Q1, Q2]), "operationType" : NewBodyOperationType.REMOVE, "endBound" : BoundingType.SYMMETRIC, "depth" : 25 * mm, "offsetDistance" : 25 * mm});
        }
        {
            var Q0;
            {var subQ1=sQuery(id+"F5.wireOp",EDGE,"E18.right");var subQ2=makeQuery(id+"F13.opExtrude","CAP_EDGE",EDGE,{"disambiguationData":[OSD([subQ1])],"isStart":true});var subQ6=sQuery(id+"F5.wireOp",EDGE,"E22");Q0=makeQuery(id+"F15.boolean.opBoolean","SPLIT",EDGE,{"disambiguationData":[TD([makeQuery(id+"F13.opExtrude","SWEPT_FACE",FACE,{"disambiguationData":[OSD([subQ6])]})])],"derivedFrom":subQ2});}
            var Q1;
            Q1=makeQuery(id+"F13.opExtrude","SWEPT_EDGE",EDGE,{"disambiguationData":[OSD([sQuery(id+"F5.wireOp",EDGE,"E18.right"),sQuery(id+"F5.wireOp",EDGE,"E22")])]});
            var Q2;
            {var subQ1=sQuery(id+"F5.wireOp",EDGE,"E18.right");var subQ5=sQuery(id+"F5.wireOp",EDGE,"E22");var subQ6=makeQuery(id+"F13.opExtrude","CAP_EDGE",EDGE,{"disambiguationData":[OSD([subQ1])],"isStart":false});Q2=makeQuery(id+"F15.boolean.opBoolean","SPLIT",EDGE,{"disambiguationData":[TD([makeQuery(id+"F13.opExtrude","SWEPT_FACE",FACE,{"disambiguationData":[OSD([subQ5])]})])],"derivedFrom":subQ6});}
            var Q3;
            Q3=makeQuery(id+"F13.opExtrude","CAP_EDGE",EDGE,{"disambiguationData":[OSD([sQuery(id+"F5.wireOp",EDGE,"E32")])],"isStart":true});
            var Q4;
            Q4=makeQuery(id+"F13.opExtrude","CAP_EDGE",EDGE,{"disambiguationData":[OSD([sQuery(id+"F5.wireOp",EDGE,"E17")])],"isStart":true});
            var Q5;
            {var subQ6=sQuery(id+"F5.wireOp",EDGE,"E18.left");var subQ7=sQuery(id+"F5.wireOp",EDGE,"E17");Q5=makeQuery(id+"F15.boolean.opBoolean","SPLIT",EDGE,{"disambiguationData":[TD([makeQuery(id+"F13.opExtrude","SWEPT_FACE",FACE,{"disambiguationData":[OSD([subQ7])]})])],"derivedFrom":makeQuery(id+"F13.opExtrude","CAP_EDGE",EDGE,{"disambiguationData":[OSD([subQ6])],"isStart":true})});}
            var Q6;
            Q6=makeQuery(id+"F13.opExtrude","CAP_EDGE",EDGE,{"disambiguationData":[OSD([sQuery(id+"F5.wireOp",EDGE,"E17")])],"isStart":false});
            var Q7;
            {var subQ0=sQuery(id+"F5.wireOp",EDGE,"E18.left");var subQ7=sQuery(id+"F5.wireOp",EDGE,"E17");Q7=makeQuery(id+"F15.boolean.opBoolean","SPLIT",EDGE,{"disambiguationData":[TD([makeQuery(id+"F13.opExtrude","SWEPT_FACE",FACE,{"disambiguationData":[OSD([subQ7])]})])],"derivedFrom":makeQuery(id+"F13.opExtrude","CAP_EDGE",EDGE,{"disambiguationData":[OSD([subQ0])],"isStart":false})});}
            var Q8;
            Q8=makeQuery(id+"F13.opExtrude","CAP_EDGE",EDGE,{"disambiguationData":[OSD([sQuery(id+"F5.wireOp",EDGE,"E32")])],"isStart":false});
            var Q9;
            Q9=makeQuery(id+"F23.opExtrude","CAP_EDGE",EDGE,{"disambiguationData":[OSD([sQuery(id+"F22.wireOp",EDGE,"E43")])],"isStart":true});
            var Q10;
            Q10=makeQuery(id+"F23.boolean.opBoolean","MERGE",EDGE,{"derivedFrom":[makeQuery(id+"F13.opExtrude","SWEPT_EDGE",EDGE,{"disambiguationData":[OSD([sQuery(id+"F5.wireOp",EDGE,"E32"),sQuery(id+"F5.wireOp",EDGE,"E33")])]}),makeQuery(id+"F23.opExtrude","CAP_EDGE",EDGE,{"disambiguationData":[OSD([sQuery(id+"F22.wireOp",EDGE,"E44")])],"isStart":true}),makeQuery(id+"F23.opExtrude","CAP_EDGE",EDGE,{"disambiguationData":[OSD([sQuery(id+"F22.wireOp",EDGE,"E46")])],"isStart":true})]});
            var Q11;
            Q11=makeQuery(id+"F23.opExtrude","CAP_EDGE",EDGE,{"disambiguationData":[OSD([sQuery(id+"F22.wireOp",EDGE,"E45")])],"isStart":true});
            var Q12;
            Q12=makeQuery(id+"F23.opExtrude","SWEPT_EDGE",EDGE,{"disambiguationData":[OSD([sQuery(id+"F22.wireOp",EDGE,"E45"),sQuery(id+"F22.wireOp",EDGE,"E46")])]});
            var Q13;
            Q13=makeQuery(id+"F23.opExtrude","SWEPT_EDGE",EDGE,{"disambiguationData":[OSD([sQuery(id+"F22.wireOp",EDGE,"E43"),sQuery(id+"F22.wireOp",EDGE,"E44")])]});
            var Q14;
            Q14=makeQuery(id+"F23.boolean.opBoolean","MERGE",EDGE,{"derivedFrom":[makeQuery(id+"F13.opExtrude","SWEPT_EDGE",EDGE,{"disambiguationData":[OSD([sQuery(id+"F5.wireOp",EDGE,"E21.top"),sQuery(id+"F5.wireOp",EDGE,"E21.left")])]}),makeQuery(id+"F23.opExtrude","CAP_EDGE",EDGE,{"disambiguationData":[OSD([sQuery(id+"F22.wireOp",EDGE,"E44")])],"isStart":false}),makeQuery(id+"F23.opExtrude","CAP_EDGE",EDGE,{"disambiguationData":[OSD([sQuery(id+"F22.wireOp",EDGE,"E46")])],"isStart":false})]});
            var Q15;
            Q15=makeQuery(id+"F25.opExtrude","CAP_EDGE",EDGE,{"disambiguationData":[OSD([sQuery(id+"F24.wireOp",EDGE,"E47.left")])],"isStart":false});
            var Q16;
            {var subQ0=sQuery(id+"F5.wireOp",EDGE,"E22");Q16=makeQuery(id+"F23.boolean.opBoolean","SPLIT",EDGE,{"disambiguationData":[topologyDisambiguationEdgeConnected([makeQuery(id+"F13.opExtrude","CAP_FACE",FACE,{"disambiguationData":[OSD([sQuery(id+"F5.wireOp",EDGE,"E17"),sQuery(id+"F5.wireOp",EDGE,"E18.bottom"),sQuery(id+"F5.wireOp",EDGE,"E18.left"),sQuery(id+"F5.wireOp",EDGE,"E18.right"),sQuery(id+"F5.wireOp",EDGE,"E19"),sQuery(id+"F5.wireOp",EDGE,"E20.right"),sQuery(id+"F5.wireOp",EDGE,"E21.top"),sQuery(id+"F5.wireOp",EDGE,"E21.left"),sQuery(id+"F5.wireOp",EDGE,"E21.right"),subQ0,sQuery(id+"F5.wireOp",EDGE,"E23.left"),sQuery(id+"F5.wireOp",EDGE,"E23.right"),sQuery(id+"F5.wireOp",EDGE,"E31"),sQuery(id+"F5.wireOp",EDGE,"E32"),sQuery(id+"F5.wireOp",EDGE,"E33")])],"isStart":false})])],"derivedFrom":makeQuery(id+"F13.opExtrude","CAP_EDGE",EDGE,{"disambiguationData":[OSD([subQ0])],"isStart":false})});}
            var Q17;
            {var subQ0=sQuery(id+"F14.wireOp",EDGE,"E41");var subQ1=makeQuery(id+"F13.opExtrude","CAP_EDGE",EDGE,{"disambiguationData":[OSD([sQuery(id+"F5.wireOp",EDGE,"E18.right")])],"isStart":true});Q17=makeQuery(id+"F15.opExtrude","CAP_EDGE",EDGE,{"disambiguationData":[OSD([subQ0]),TDD([makeQuery(id+"F14.imprint","IMPRINT",EDGE,{"disambiguationData":[TD([[makeQuery(id+"F14.imprint","INTERSECT",VERTEX,{"disambiguationData":[OD(0.0)],"derivedFrom":[subQ1,subQ0]}),-1.0]])],"derivedFrom":subQ0})])],"isStart":true});}
            var Q18;
            {var subQ0=sQuery(id+"F5.wireOp",EDGE,"E18.right");var subQ5=makeQuery(id+"F13.opExtrude","CAP_EDGE",EDGE,{"disambiguationData":[OSD([subQ0])],"isStart":true});var subQ9=sQuery(id+"F5.wireOp",EDGE,"E18.bottom");Q18=makeQuery(id+"F15.boolean.opBoolean","SPLIT",EDGE,{"disambiguationData":[TD([makeQuery(id+"F13.opExtrude","SWEPT_FACE",FACE,{"disambiguationData":[OSD([subQ9])]})])],"derivedFrom":subQ5});}
            var Q19;
            {var subQ0=sQuery(id+"F14.wireOp",EDGE,"E41");var subQ1=sQuery(id+"F5.wireOp",EDGE,"E18.right");Q19=makeQuery(id+"F15.opExtrude","SWEPT_EDGE",EDGE,{"disambiguationData":[OSD([subQ1,subQ0]),TDD([makeQuery(id+"F14.imprint","INTERSECT",VERTEX,{"disambiguationData":[OD(0.0)],"derivedFrom":[makeQuery(id+"F13.opExtrude","CAP_EDGE",EDGE,{"disambiguationData":[OSD([subQ1])],"isStart":true}),subQ0]})])]});}
            var Q20;
            {var subQ0=sQuery(id+"F5.wireOp",EDGE,"E18.left");var subQ7=sQuery(id+"F5.wireOp",EDGE,"E18.bottom");Q20=makeQuery(id+"F15.boolean.opBoolean","SPLIT",EDGE,{"disambiguationData":[TD([makeQuery(id+"F13.opExtrude","SWEPT_FACE",FACE,{"disambiguationData":[OSD([subQ7])]})])],"derivedFrom":makeQuery(id+"F13.opExtrude","CAP_EDGE",EDGE,{"disambiguationData":[OSD([subQ0])],"isStart":true})});}
            var Q21;
            {var subQ0=sQuery(id+"F14.wireOp",EDGE,"E41");var subQ1=makeQuery(id+"F13.opExtrude","CAP_EDGE",EDGE,{"disambiguationData":[OSD([sQuery(id+"F5.wireOp",EDGE,"E18.right")])],"isStart":true});Q21=makeQuery(id+"F15.opExtrude","CAP_EDGE",EDGE,{"disambiguationData":[OSD([subQ0]),TDD([makeQuery(id+"F14.imprint","IMPRINT",EDGE,{"disambiguationData":[TD([[makeQuery(id+"F14.imprint","INTERSECT",VERTEX,{"disambiguationData":[OD(0.0)],"derivedFrom":[subQ1,subQ0]}),-1.0]])],"derivedFrom":subQ0})])],"isStart":false});}
            var Q22;
            {var subQ0=sQuery(id+"F14.wireOp",EDGE,"E41");var subQ1=makeQuery(id+"F13.opExtrude","CAP_EDGE",EDGE,{"disambiguationData":[OSD([sQuery(id+"F5.wireOp",EDGE,"E18.right")])],"isStart":false});Q22=makeQuery(id+"F15.opExtrude","CAP_EDGE",EDGE,{"disambiguationData":[OSD([subQ0]),TDD([makeQuery(id+"F14.imprint","IMPRINT",EDGE,{"disambiguationData":[TD([[makeQuery(id+"F14.imprint","INTERSECT",VERTEX,{"disambiguationData":[OD(0.0)],"derivedFrom":[subQ1,subQ0]}),1.0]])],"derivedFrom":subQ0})])],"isStart":true});}
            var Q23;
            {var subQ1=sQuery(id+"F5.wireOp",EDGE,"E18.right");var subQ5=sQuery(id+"F5.wireOp",EDGE,"E18.bottom");var subQ6=makeQuery(id+"F13.opExtrude","CAP_EDGE",EDGE,{"disambiguationData":[OSD([subQ1])],"isStart":false});Q23=makeQuery(id+"F15.boolean.opBoolean","SPLIT",EDGE,{"disambiguationData":[TD([makeQuery(id+"F13.opExtrude","SWEPT_FACE",FACE,{"disambiguationData":[OSD([subQ5])]})])],"derivedFrom":subQ6});}
            var Q24;
            Q24=makeQuery(id+"F13.opExtrude","CAP_EDGE",EDGE,{"disambiguationData":[OSD([sQuery(id+"F5.wireOp",EDGE,"E18.bottom")])],"isStart":false});
            var Q25;
            {var subQ0=sQuery(id+"F14.wireOp",EDGE,"E41");var subQ1=makeQuery(id+"F13.opExtrude","CAP_EDGE",EDGE,{"disambiguationData":[OSD([sQuery(id+"F5.wireOp",EDGE,"E18.right")])],"isStart":false});Q25=makeQuery(id+"F15.opExtrude","CAP_EDGE",EDGE,{"disambiguationData":[OSD([subQ0]),TDD([makeQuery(id+"F14.imprint","IMPRINT",EDGE,{"disambiguationData":[TD([[makeQuery(id+"F14.imprint","INTERSECT",VERTEX,{"disambiguationData":[OD(0.0)],"derivedFrom":[subQ1,subQ0]}),1.0]])],"derivedFrom":subQ0})])],"isStart":false});}
            var Q26;
            {var subQ1=sQuery(id+"F5.wireOp",EDGE,"E18.right");var subQ8=sQuery(id+"F5.wireOp",EDGE,"E18.bottom");Q26=makeQuery(id+"F16.boolean.opBoolean","SPLIT",EDGE,{"disambiguationData":[TD([makeQuery(id+"F16.opExtrude","SWEPT_FACE",FACE,{"disambiguationData":[OSD([sQuery(id+"F14.wireOp",EDGE,"E37.left")])]})])],"derivedFrom":makeQuery(id+"F13.opExtrude","SWEPT_EDGE",EDGE,{"disambiguationData":[OSD([subQ8,subQ1])]})});}
            var Q27;
            {var subQ1=sQuery(id+"F5.wireOp",EDGE,"E18.right");var subQ5=sQuery(id+"F5.wireOp",EDGE,"E18.bottom");Q27=makeQuery(id+"F16.boolean.opBoolean","SPLIT",EDGE,{"disambiguationData":[TD([makeQuery(id+"F16.opExtrude","SWEPT_FACE",FACE,{"disambiguationData":[OSD([sQuery(id+"F14.wireOp",EDGE,"E37.right")])]})])],"derivedFrom":makeQuery(id+"F13.opExtrude","SWEPT_EDGE",EDGE,{"disambiguationData":[OSD([subQ5,subQ1])]})});}
            var Q28;
            {var subQ5=sQuery(id+"F5.wireOp",EDGE,"E18.bottom");var subQ6=sQuery(id+"F5.wireOp",EDGE,"E18.left");Q28=makeQuery(id+"F16.boolean.opBoolean","SPLIT",EDGE,{"disambiguationData":[TD([makeQuery(id+"F16.opExtrude","SWEPT_FACE",FACE,{"disambiguationData":[OSD([sQuery(id+"F14.wireOp",EDGE,"E37.left")])]})])],"derivedFrom":makeQuery(id+"F13.opExtrude","SWEPT_EDGE",EDGE,{"disambiguationData":[OSD([subQ5,subQ6])]})});}
            var Q29;
            {var subQ5=sQuery(id+"F5.wireOp",EDGE,"E18.bottom");var subQ6=sQuery(id+"F5.wireOp",EDGE,"E18.left");Q29=makeQuery(id+"F16.boolean.opBoolean","SPLIT",EDGE,{"disambiguationData":[TD([makeQuery(id+"F16.opExtrude","SWEPT_FACE",FACE,{"disambiguationData":[OSD([sQuery(id+"F14.wireOp",EDGE,"E37.right")])]})])],"derivedFrom":makeQuery(id+"F13.opExtrude","SWEPT_EDGE",EDGE,{"disambiguationData":[OSD([subQ5,subQ6])]})});}
            var Q30;
            {var subQ5=sQuery(id+"F5.wireOp",EDGE,"E18.bottom");var subQ6=sQuery(id+"F5.wireOp",EDGE,"E18.left");Q30=makeQuery(id+"F15.boolean.opBoolean","SPLIT",EDGE,{"disambiguationData":[TD([makeQuery(id+"F13.opExtrude","SWEPT_FACE",FACE,{"disambiguationData":[OSD([subQ5])]})])],"derivedFrom":makeQuery(id+"F13.opExtrude","CAP_EDGE",EDGE,{"disambiguationData":[OSD([subQ6])],"isStart":false})});}
            fillet(context, id + "F27", {"entities" : qUnion([Q0, Q1, Q2, Q3, Q4, Q5, Q6, Q7, Q8, Q9, Q10, Q11, Q12, Q13, Q14, Q15, Q16, Q17, Q18, Q19, Q20, Q21, Q22, Q23, Q24, Q25, Q26, Q27, Q28, Q29, Q30]), "radius" : 1 * mm, "tangentPropagation" : true, "allowEdgeOverflow" : false});
        }
    });
